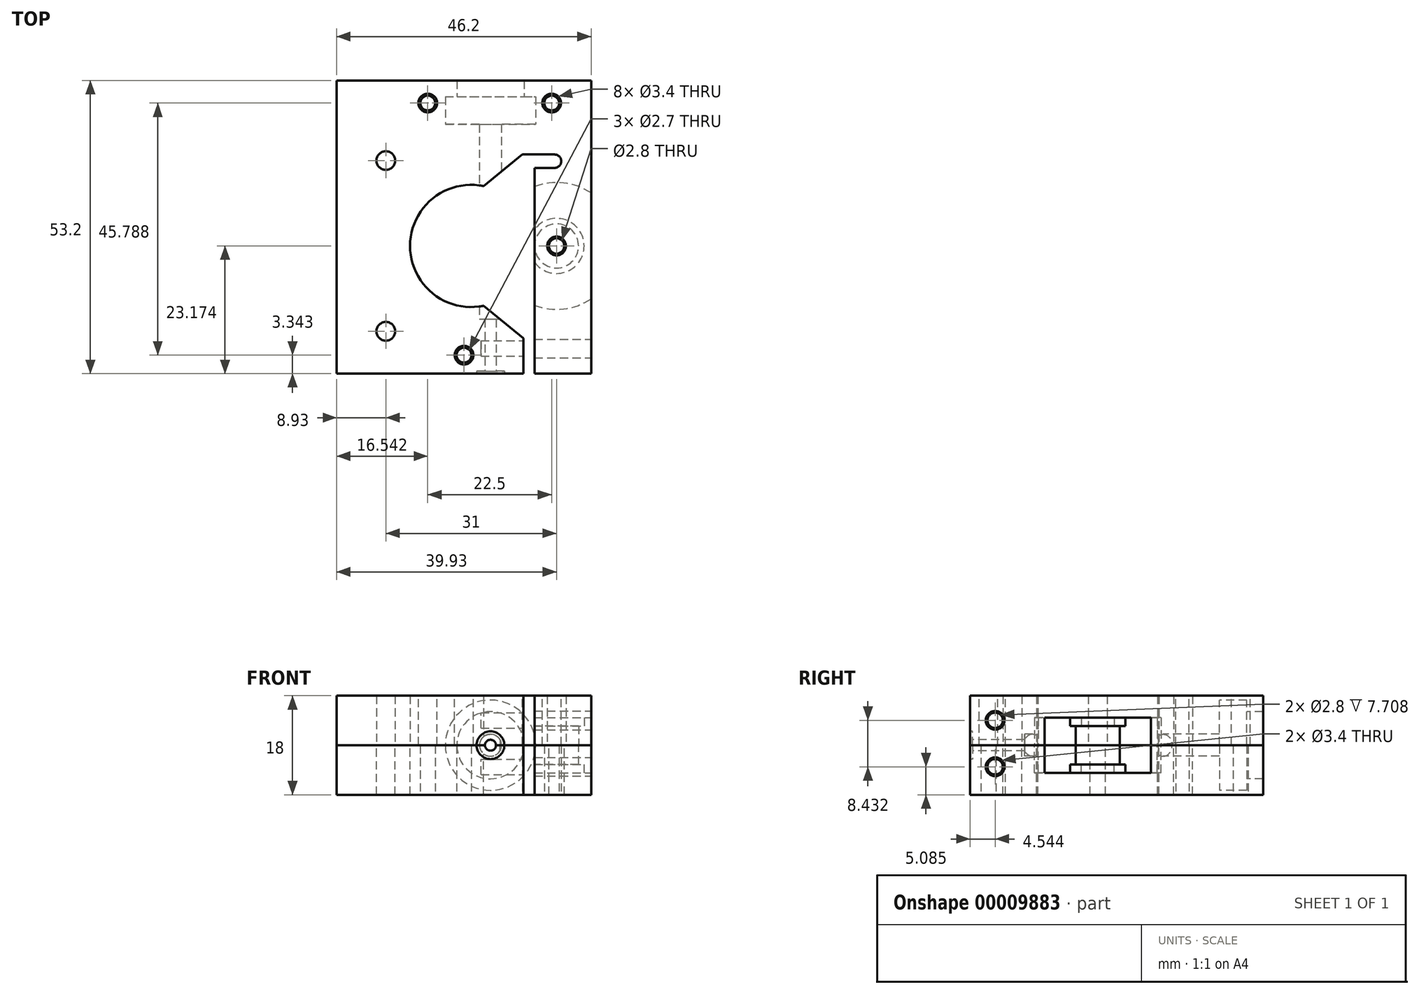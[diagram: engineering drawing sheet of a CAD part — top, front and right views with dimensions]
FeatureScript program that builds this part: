
annotation { "Feature Type Name" : "Feature", "Feature Type Description" : "" }
export const myFeature = defineFeature(function(context is Context, id is Id, definition is map)
    precondition{}
    {
        {
            var Q0;
            Q0=qCreatedBy(makeId("Top.planeOp"),FACE);
            var sketch = newSketch(context, id + "F0", { "sketchPlane" : qUnion([Q0])});
            skLineSegment(sketch, "E0", {"start": v(-24.43, 35.85) * mm, "end": v(-24.43, -17.36) * mm});
            skLineSegment(sketch, "E1", {"start": v(-24.43, -17.36) * mm, "end": v(-24.43, -17.36) * mm});
            skLineSegment(sketch, "E2", {"start": v(-24.43, -17.36) * mm, "end": v(-24.43, -17.35) * mm});
            skLineSegment(sketch, "E3", {"start": v(-24.43, -17.35) * mm, "end": v(9.48, -17.35) * mm});
            skLineSegment(sketch, "E4", {"start": v(9.48, -17.35) * mm, "end": v(9.48, 22.43) * mm});
            skLineSegment(sketch, "E5", {"start": v(9.48, 22.43) * mm, "end": v(15.14, 22.43) * mm});
            skLineSegment(sketch, "E6", {"start": v(15.14, 20) * mm, "end": v(11.48, 20) * mm});
            skLineSegment(sketch, "E7", {"start": v(11.48, 20) * mm, "end": v(11.48, -17.35) * mm});
            skLineSegment(sketch, "E8", {"start": v(11.48, -17.35) * mm, "end": v(21.77, -17.35) * mm});
            skLineSegment(sketch, "E9", {"start": v(21.77, -17.35) * mm, "end": v(21.77, 35.85) * mm});
            skLineSegment(sketch, "E10", {"start": v(21.77, 35.85) * mm, "end": v(-24.43, 35.85) * mm});
            skCircle(sketch, "E11", {"center": v(-7.89, 31.78) * mm, "radius": 1.35 * mm});
            skCircle(sketch, "E12", {"center": v(14.61, 31.78) * mm, "radius": 1.35 * mm});
            skCircle(sketch, "E13", {"center": v(-1.3, -14) * mm, "radius": 1.35 * mm});
            skArc(sketch, "E14", {"start": v(15.14, 20) * mm, "mid": v(16.35, 21.21) * mm, "end": v(15.14, 22.43) * mm});
            skCircle(sketch, "E15", {"center": v(-7.89, 31.78) * mm, "radius": 1.7 * mm});
            skCircle(sketch, "E16", {"center": v(14.61, 31.78) * mm, "radius": 1.7 * mm});
            skCircle(sketch, "E17", {"center": v(-1.3, -14) * mm, "radius": 1.7 * mm});
            skSolve(sketch);
        }
        {
            var Q0;
            Q0=makeQuery(id+"F0.imprint","IMPRINT",FACE,{"disambiguationData":[TD([[makeQuery(id+"F0.imprint","IMPRINT",EDGE,{"derivedFrom":sQuery(id+"F0.wireOp",EDGE,"E0")}),1.0]])]});
            var Q1;
            Q1=makeQuery(id+"F0.imprint","IMPRINT",FACE,{"disambiguationData":[TD([[makeQuery(id+"F0.imprint","IMPRINT",EDGE,{"derivedFrom":sQuery(id+"F0.wireOp",EDGE,"E11")}),-1.0]])]});
            var Q2;
            Q2=makeQuery(id+"F0.imprint","IMPRINT",FACE,{"disambiguationData":[TD([[makeQuery(id+"F0.imprint","IMPRINT",EDGE,{"derivedFrom":sQuery(id+"F0.wireOp",EDGE,"E12")}),-1.0]])]});
            var Q3;
            Q3=makeQuery(id+"F0.imprint","IMPRINT",FACE,{"disambiguationData":[TD([[makeQuery(id+"F0.imprint","IMPRINT",EDGE,{"derivedFrom":sQuery(id+"F0.wireOp",EDGE,"E13")}),-1.0]])]});
            extrude(context, id + "F1", {"entities" : qUnion([Q0, Q1, Q2, Q3]), "depth" : 9 * mm});
        }
        {
            var Q0;
            Q0=makeQuery(id+"F1.opExtrude","CAP_FACE",FACE,{"disambiguationData":[OSD([sQuery(id+"F0.wireOp",EDGE,"E0"),sQuery(id+"F0.wireOp",EDGE,"E1"),sQuery(id+"F0.wireOp",EDGE,"E2"),sQuery(id+"F0.wireOp",EDGE,"E3"),sQuery(id+"F0.wireOp",EDGE,"E4"),sQuery(id+"F0.wireOp",EDGE,"E5"),sQuery(id+"F0.wireOp",EDGE,"E6"),sQuery(id+"F0.wireOp",EDGE,"E7"),sQuery(id+"F0.wireOp",EDGE,"E8"),sQuery(id+"F0.wireOp",EDGE,"E9"),sQuery(id+"F0.wireOp",EDGE,"E10"),sQuery(id+"F0.wireOp",EDGE,"604cad85-587a-4b7d-8070-06f4cba85480"),sQuery(id+"F0.wireOp",EDGE,"6e5e38c1-5bff-4efe-a8c5-b84022f0a049"),sQuery(id+"F0.wireOp",EDGE,"b8144507-9dd7-4af4-87a3-7b649dd00ae6"),sQuery(id+"F0.wireOp",EDGE,"b9c2cb7c-5e58-4995-888e-a78f0403fbb5"),sQuery(id+"F0.wireOp",EDGE,"885990ab-7576-4c23-8475-595d2769e284"),sQuery(id+"F0.wireOp",EDGE,"E11"),sQuery(id+"F0.wireOp",EDGE,"E12"),sQuery(id+"F0.wireOp",EDGE,"E13"),sQuery(id+"F0.wireOp",EDGE,"E14")])],"isStart":false});
            var sketch = newSketch(context, id + "F2", { "sketchPlane" : qUnion([Q0])});
            skCircle(sketch, "E18", {"center": v(0, 5.82) * mm, "radius": 11.1 * mm});
            skCircle(sketch, "E19", {"center": v(-15.5, 21.32) * mm, "radius": 1.7 * mm});
            skCircle(sketch, "E20", {"center": v(-15.5, -9.68) * mm, "radius": 1.7 * mm});
            skSolve(sketch);
        }
        {
            var Q0;
            Q0=qSketchRegion(id+"F2",true);
            extrude(context, id + "F3", {"entities" : qUnion([Q0]), "operationType" : NewBodyOperationType.REMOVE, "endBound" : BoundingType.THROUGH_ALL, "oppositeDirection" : true, "depth" : 25 * mm});
        }
        {
            var Q0;
            Q0=makeQuery(id+"F1.opExtrude","CAP_FACE",FACE,{"disambiguationData":[OSD([sQuery(id+"F0.wireOp",EDGE,"E0"),sQuery(id+"F0.wireOp",EDGE,"E1"),sQuery(id+"F0.wireOp",EDGE,"E2"),sQuery(id+"F0.wireOp",EDGE,"E3"),sQuery(id+"F0.wireOp",EDGE,"E4"),sQuery(id+"F0.wireOp",EDGE,"E5"),sQuery(id+"F0.wireOp",EDGE,"E6"),sQuery(id+"F0.wireOp",EDGE,"E7"),sQuery(id+"F0.wireOp",EDGE,"E8"),sQuery(id+"F0.wireOp",EDGE,"E9"),sQuery(id+"F0.wireOp",EDGE,"E10"),sQuery(id+"F0.wireOp",EDGE,"604cad85-587a-4b7d-8070-06f4cba85480"),sQuery(id+"F0.wireOp",EDGE,"6e5e38c1-5bff-4efe-a8c5-b84022f0a049"),sQuery(id+"F0.wireOp",EDGE,"E11"),sQuery(id+"F0.wireOp",EDGE,"E12"),sQuery(id+"F0.wireOp",EDGE,"E13"),sQuery(id+"F0.wireOp",EDGE,"E14")])],"isStart":false});
            var sketch = newSketch(context, id + "F4", { "sketchPlane" : qUnion([Q0])});
            skCircle(sketch, "E21", {"center": v(15.5, 5.82) * mm, "radius": 11.5 * mm});
            skCircle(sketch, "E22", {"center": v(15.5, 5.82) * mm, "radius": 5 * mm});
            skCircle(sketch, "E23", {"center": v(15.5, 5.82) * mm, "radius": 4 * mm});
            skLineSegment(sketch, "E24", {"start": v(0, 5.82) * mm, "end": v(31, 5.82) * mm, "construction": true});
            skCircle(sketch, "E25", {"center": v(15.5, 5.82) * mm, "radius": 1.4 * mm});
            skCircle(sketch, "E26", {"center": v(15.5, 5.82) * mm, "radius": 1.7 * mm});
            skSolve(sketch);
        }
        {
            var Q0;
            Q0=makeQuery(id+"F4.imprint","IMPRINT",FACE,{"disambiguationData":[TD([[makeQuery(id+"F4.imprint","IMPRINT",EDGE,{"derivedFrom":sQuery(id+"F4.wireOp",EDGE,"E22")}),-1.0]])]});
            extrude(context, id + "F5", {"entities" : qUnion([Q0]), "operationType" : NewBodyOperationType.REMOVE, "oppositeDirection" : true, "depth" : 5 * mm});
        }
        {
            var Q0;
            Q0=makeQuery(id+"F4.imprint","IMPRINT",FACE,{"disambiguationData":[TD([[makeQuery(id+"F4.imprint","IMPRINT",EDGE,{"derivedFrom":sQuery(id+"F4.wireOp",EDGE,"E22")}),1.0]])]});
            var Q1;
            Q1=makeQuery(id+"F4.imprint","IMPRINT",FACE,{"disambiguationData":[TD([[makeQuery(id+"F4.imprint","IMPRINT",EDGE,{"derivedFrom":sQuery(id+"F4.wireOp",EDGE,"E23")}),-1.0]])]});
            extrude(context, id + "F6", {"entities" : qUnion([Q0, Q1]), "operationType" : NewBodyOperationType.REMOVE, "oppositeDirection" : true, "depth" : 3.5 * mm});
        }
        {
            var Q0;
            {var subQ0=sQuery(id+"F0.wireOp",EDGE,"E0");var subQ1=sQuery(id+"F0.wireOp",EDGE,"E1");var subQ2=sQuery(id+"F0.wireOp",EDGE,"E2");var subQ3=sQuery(id+"F0.wireOp",EDGE,"E3");var subQ4=sQuery(id+"F0.wireOp",EDGE,"E4");var subQ5=sQuery(id+"F0.wireOp",EDGE,"E5");var subQ6=sQuery(id+"F0.wireOp",EDGE,"E6");var subQ7=sQuery(id+"F0.wireOp",EDGE,"E7");var subQ8=sQuery(id+"F0.wireOp",EDGE,"E9");var subQ9=sQuery(id+"F0.wireOp",EDGE,"E10");var subQ10=sQuery(id+"F0.wireOp",EDGE,"604cad85-587a-4b7d-8070-06f4cba85480");var subQ11=sQuery(id+"F0.wireOp",EDGE,"6e5e38c1-5bff-4efe-a8c5-b84022f0a049");var subQ12=sQuery(id+"F0.wireOp",EDGE,"E11");var subQ13=sQuery(id+"F0.wireOp",EDGE,"E12");var subQ14=sQuery(id+"F0.wireOp",EDGE,"E13");var subQ15=sQuery(id+"F0.wireOp",EDGE,"E14");Q0=makeQuery(id+"F5.boolean.opBoolean","SPLIT",FACE,{"disambiguationData":[TD([makeQuery(id+"F1.opExtrude","SWEPT_FACE",FACE,{"disambiguationData":[OSD([subQ0])]})])],"derivedFrom":makeQuery(id+"F1.opExtrude","CAP_FACE",FACE,{"disambiguationData":[OSD([subQ0,subQ1,subQ2,subQ3,subQ4,subQ5,subQ6,subQ7,sQuery(id+"F0.wireOp",EDGE,"E8"),subQ8,subQ9,subQ10,subQ11,subQ12,subQ13,subQ14,subQ15])],"isStart":false})});}
            var sketch = newSketch(context, id + "F7", { "sketchPlane" : qUnion([Q0])});
            skLineSegment(sketch, "E27", {"start": v(3.5, 15.43) * mm, "end": v(3.5, 37.1) * mm});
            skLineSegment(sketch, "E28", {"start": v(0, 5.82) * mm, "end": v(31.4, 5.82) * mm, "construction": true});
            skLineSegment(sketch, "E29.0.MirrorCS", {"start": v(0.98, -16.94) * mm, "end": v(2.5, -16.94) * mm});
            skLineSegment(sketch, "E29.1.MirrorCS", {"start": v(3.5, -3.78) * mm, "end": v(3.5, -25.46) * mm});
            skLineSegment(sketch, "E29.2.MirrorCS", {"start": v(0.98, -25.46) * mm, "end": v(0.98, -16.94) * mm});
            skLineSegment(sketch, "E29.3.MirrorCS", {"start": v(1.5, -3.78) * mm, "end": v(3.5, -3.78) * mm});
            skLineSegment(sketch, "E29.4.MirrorCS", {"start": v(2.5, -7.47) * mm, "end": v(1.5, -7.47) * mm});
            skLineSegment(sketch, "E29.5.MirrorCS", {"start": v(2.5, -16.94) * mm, "end": v(2.5, -7.47) * mm});
            skLineSegment(sketch, "E29.6.MirrorCS", {"start": v(3.5, -25.46) * mm, "end": v(0.98, -25.46) * mm});
            skLineSegment(sketch, "E30", {"start": v(-2.6, 37.1) * mm, "end": v(-2.6, 32.9) * mm});
            skLineSegment(sketch, "E31", {"start": v(-2.6, 32.9) * mm, "end": v(-4.7, 32.9) * mm});
            skLineSegment(sketch, "E32", {"start": v(-4.7, 32.9) * mm, "end": v(-4.7, 27.9) * mm});
            skLineSegment(sketch, "E33", {"start": v(-4.7, 27.9) * mm, "end": v(1.5, 27.9) * mm});
            skLineSegment(sketch, "E34", {"start": v(-2.6, 37.1) * mm, "end": v(3.5, 37.1) * mm});
            skLineSegment(sketch, "E35", {"start": v(1.5, 27.9) * mm, "end": v(1.5, 15.43) * mm});
            skLineSegment(sketch, "E36", {"start": v(1.5, 15.43) * mm, "end": v(3.5, 15.43) * mm});
            skLineSegment(sketch, "E37", {"start": v(1.5, -7.47) * mm, "end": v(1.5, -3.78) * mm});
            skSolve(sketch);
        }
        {
            var Q0;
            Q0=qSketchRegion(id+"F7",true);
            var Q1;
            Q1=sQuery(id+"F7.wireOp",EDGE,"E27");
            revolve(context, id + "F8", {"entities" : qUnion([Q0]), "axis" : qUnion([Q1]), "revolveType" : RevolveType.FULL});
        }
        {
            var Q0;
            Q0=makeQuery(id+"F8.opRevolve","SWEPT_BODY",BODY,{"disambiguationData":[OSD([sQuery(id+"F7.wireOp",EDGE,"0e4a01cc-4869-4b9d-8ca2-1c94110d196d"),sQuery(id+"F7.wireOp",EDGE,"4d913e13-2244-4a79-84d2-82f6c5de00b3"),sQuery(id+"F7.wireOp",EDGE,"1203443b-fa58-4cec-9fe4-144960d3b7c2"),sQuery(id+"F7.wireOp",EDGE,"f73e5a92-9274-40af-91db-ab5fa52ec61f"),sQuery(id+"F7.wireOp",EDGE,"4cc6588a-36a6-4115-9f4e-735cf5f17870"),sQuery(id+"F7.wireOp",EDGE,"E27"),sQuery(id+"F7.wireOp",EDGE,"0bbee7b9-97e0-41c3-ac0e-625151f8027d")])]});
            var Q1;
            Q1=makeQuery(id+"F1.opExtrude","SWEPT_BODY",BODY,{"disambiguationData":[OSD([sQuery(id+"F0.wireOp",EDGE,"E0"),sQuery(id+"F0.wireOp",EDGE,"E1"),sQuery(id+"F0.wireOp",EDGE,"E2"),sQuery(id+"F0.wireOp",EDGE,"E3"),sQuery(id+"F0.wireOp",EDGE,"E4"),sQuery(id+"F0.wireOp",EDGE,"E5"),sQuery(id+"F0.wireOp",EDGE,"E6"),sQuery(id+"F0.wireOp",EDGE,"E7"),sQuery(id+"F0.wireOp",EDGE,"E8"),sQuery(id+"F0.wireOp",EDGE,"E9"),sQuery(id+"F0.wireOp",EDGE,"E10"),sQuery(id+"F0.wireOp",EDGE,"604cad85-587a-4b7d-8070-06f4cba85480"),sQuery(id+"F0.wireOp",EDGE,"6e5e38c1-5bff-4efe-a8c5-b84022f0a049"),sQuery(id+"F0.wireOp",EDGE,"E11"),sQuery(id+"F0.wireOp",EDGE,"E12"),sQuery(id+"F0.wireOp",EDGE,"E13"),sQuery(id+"F0.wireOp",EDGE,"E14")])]});
            booleanBodies(context, id + "F9", {"operationType" : BooleanOperationType.SUBTRACTION, "tools" : qUnion([Q0]), "targets" : qUnion([Q1]), "keepTools" : true});
        }
        {
            var Q0;
            Q0=makeQuery(id+"F8.opRevolve","SWEPT_BODY",BODY,{"disambiguationData":[OSD([sQuery(id+"F7.wireOp",EDGE,"E29.0.MirrorCS"),sQuery(id+"F7.wireOp",EDGE,"E29.1.MirrorCS"),sQuery(id+"F7.wireOp",EDGE,"E29.2.MirrorCS"),sQuery(id+"F7.wireOp",EDGE,"E29.3.MirrorCS"),sQuery(id+"F7.wireOp",EDGE,"E29.4.MirrorCS"),sQuery(id+"F7.wireOp",EDGE,"E29.5.MirrorCS"),sQuery(id+"F7.wireOp",EDGE,"E29.6.MirrorCS")])]});
            var Q1;
            Q1=makeQuery(id+"F1.opExtrude","SWEPT_BODY",BODY,{"disambiguationData":[OSD([sQuery(id+"F0.wireOp",EDGE,"E0"),sQuery(id+"F0.wireOp",EDGE,"E1"),sQuery(id+"F0.wireOp",EDGE,"E2"),sQuery(id+"F0.wireOp",EDGE,"E3"),sQuery(id+"F0.wireOp",EDGE,"E4"),sQuery(id+"F0.wireOp",EDGE,"E5"),sQuery(id+"F0.wireOp",EDGE,"E6"),sQuery(id+"F0.wireOp",EDGE,"E7"),sQuery(id+"F0.wireOp",EDGE,"E8"),sQuery(id+"F0.wireOp",EDGE,"E9"),sQuery(id+"F0.wireOp",EDGE,"E10"),sQuery(id+"F0.wireOp",EDGE,"604cad85-587a-4b7d-8070-06f4cba85480"),sQuery(id+"F0.wireOp",EDGE,"6e5e38c1-5bff-4efe-a8c5-b84022f0a049"),sQuery(id+"F0.wireOp",EDGE,"E11"),sQuery(id+"F0.wireOp",EDGE,"E12"),sQuery(id+"F0.wireOp",EDGE,"E13"),sQuery(id+"F0.wireOp",EDGE,"E14")])]});
            booleanBodies(context, id + "F10", {"operationType" : BooleanOperationType.SUBTRACTION, "tools" : qUnion([Q0]), "targets" : qUnion([Q1]), "keepTools" : true});
        }
        {
            var Q0;
            Q0=qSketchRegion(id+"F0",true);
            extrude(context, id + "F11", {"entities" : qUnion([Q0]), "oppositeDirection" : true, "depth" : 9 * mm});
        }
        {
            var Q0;
            Q0=makeQuery(id+"F11.opExtrude","SWEPT_BODY",BODY,{"disambiguationData":[OSD([sQuery(id+"F0.wireOp",EDGE,"E0"),sQuery(id+"F0.wireOp",EDGE,"E3"),sQuery(id+"F0.wireOp",EDGE,"E4"),sQuery(id+"F0.wireOp",EDGE,"E5"),sQuery(id+"F0.wireOp",EDGE,"E6"),sQuery(id+"F0.wireOp",EDGE,"E7"),sQuery(id+"F0.wireOp",EDGE,"E8"),sQuery(id+"F0.wireOp",EDGE,"E9"),sQuery(id+"F0.wireOp",EDGE,"E10"),sQuery(id+"F0.wireOp",EDGE,"E11"),sQuery(id+"F0.wireOp",EDGE,"E12"),sQuery(id+"F0.wireOp",EDGE,"E13"),sQuery(id+"F0.wireOp",EDGE,"E14")])]});
            transform(context, id + "F12", {"entities" : qUnion([Q0]), "transformType" : TransformType.TRANSLATION_3D, "dx" : 0 * mm, "dy" : 0 * mm, "dz" : 18 * mm, "makeCopy" : false});
        }
        {
            var Q0;
            Q0=qSketchRegion(id+"F2",true);
            extrude(context, id + "F13", {"entities" : qUnion([Q0]), "operationType" : NewBodyOperationType.REMOVE, "endBound" : BoundingType.THROUGH_ALL, "depth" : 25 * mm});
        }
        {
            var Q0;
            {var subQ3=sQuery(id+"F4.wireOp",EDGE,"E21");var subQ7=makeQuery(id+"F1.opExtrude","CAP_EDGE",EDGE,{"disambiguationData":[OSD([sQuery(id+"F0.wireOp",EDGE,"E9")])],"isStart":false});var subQ9=makeQuery(id+"F4.imprint","INTERSECT",VERTEX,{"disambiguationData":[OD(0.0)],"derivedFrom":[subQ7,subQ3]});Q0=makeQuery(id+"F4.imprint","IMPRINT",FACE,{"disambiguationData":[TD([[makeQuery(id+"F4.imprint","IMPRINT",EDGE,{"disambiguationData":[TD([[subQ9,-1.0]])],"derivedFrom":subQ3}),1.0]])]});}
            extrude(context, id + "F14", {"entities" : qUnion([Q0]), "operationType" : NewBodyOperationType.REMOVE, "depth" : 5 * mm});
        }
        {
            var Q0;
            Q0=makeQuery(id+"F4.imprint","IMPRINT",FACE,{"disambiguationData":[TD([[makeQuery(id+"F4.imprint","IMPRINT",EDGE,{"derivedFrom":sQuery(id+"F4.wireOp",EDGE,"E23")}),-1.0]])]});
            extrude(context, id + "F15", {"entities" : qUnion([Q0]), "operationType" : NewBodyOperationType.REMOVE, "depth" : 3.5 * mm});
        }
        {
            var Q0;
            Q0=makeQuery(id+"F8.opRevolve","SWEPT_BODY",BODY,{"disambiguationData":[OSD([sQuery(id+"F7.wireOp",EDGE,"0e4a01cc-4869-4b9d-8ca2-1c94110d196d"),sQuery(id+"F7.wireOp",EDGE,"4d913e13-2244-4a79-84d2-82f6c5de00b3"),sQuery(id+"F7.wireOp",EDGE,"1203443b-fa58-4cec-9fe4-144960d3b7c2"),sQuery(id+"F7.wireOp",EDGE,"f73e5a92-9274-40af-91db-ab5fa52ec61f"),sQuery(id+"F7.wireOp",EDGE,"4cc6588a-36a6-4115-9f4e-735cf5f17870"),sQuery(id+"F7.wireOp",EDGE,"E27"),sQuery(id+"F7.wireOp",EDGE,"0bbee7b9-97e0-41c3-ac0e-625151f8027d")])]});
            var Q1;
            Q1=makeQuery(id+"F11.opExtrude","SWEPT_BODY",BODY,{"disambiguationData":[OSD([sQuery(id+"F0.wireOp",EDGE,"E0"),sQuery(id+"F0.wireOp",EDGE,"E3"),sQuery(id+"F0.wireOp",EDGE,"E4"),sQuery(id+"F0.wireOp",EDGE,"E5"),sQuery(id+"F0.wireOp",EDGE,"E6"),sQuery(id+"F0.wireOp",EDGE,"E7"),sQuery(id+"F0.wireOp",EDGE,"E8"),sQuery(id+"F0.wireOp",EDGE,"E9"),sQuery(id+"F0.wireOp",EDGE,"E10"),sQuery(id+"F0.wireOp",EDGE,"E11"),sQuery(id+"F0.wireOp",EDGE,"E12"),sQuery(id+"F0.wireOp",EDGE,"E13"),sQuery(id+"F0.wireOp",EDGE,"E14")])]});
            booleanBodies(context, id + "F16", {"operationType" : BooleanOperationType.SUBTRACTION, "tools" : qUnion([Q0]), "targets" : qUnion([Q1])});
        }
        {
            var Q0;
            Q0=makeQuery(id+"F8.opRevolve","SWEPT_BODY",BODY,{"disambiguationData":[OSD([sQuery(id+"F7.wireOp",EDGE,"E29.0.MirrorCS"),sQuery(id+"F7.wireOp",EDGE,"E29.1.MirrorCS"),sQuery(id+"F7.wireOp",EDGE,"E29.2.MirrorCS"),sQuery(id+"F7.wireOp",EDGE,"E29.3.MirrorCS"),sQuery(id+"F7.wireOp",EDGE,"E29.4.MirrorCS"),sQuery(id+"F7.wireOp",EDGE,"E29.5.MirrorCS"),sQuery(id+"F7.wireOp",EDGE,"E29.6.MirrorCS")])]});
            var Q1;
            Q1=makeQuery(id+"F11.opExtrude","SWEPT_BODY",BODY,{"disambiguationData":[OSD([sQuery(id+"F0.wireOp",EDGE,"E0"),sQuery(id+"F0.wireOp",EDGE,"E3"),sQuery(id+"F0.wireOp",EDGE,"E4"),sQuery(id+"F0.wireOp",EDGE,"E5"),sQuery(id+"F0.wireOp",EDGE,"E6"),sQuery(id+"F0.wireOp",EDGE,"E7"),sQuery(id+"F0.wireOp",EDGE,"E8"),sQuery(id+"F0.wireOp",EDGE,"E9"),sQuery(id+"F0.wireOp",EDGE,"E10"),sQuery(id+"F0.wireOp",EDGE,"E11"),sQuery(id+"F0.wireOp",EDGE,"E12"),sQuery(id+"F0.wireOp",EDGE,"E13"),sQuery(id+"F0.wireOp",EDGE,"E14")])]});
            booleanBodies(context, id + "F17", {"operationType" : BooleanOperationType.SUBTRACTION, "tools" : qUnion([Q0]), "targets" : qUnion([Q1])});
        }
        {
            var Q0;
            Q0=makeQuery(id+"F11.opExtrude","SWEPT_FACE",FACE,{"disambiguationData":[OSD([sQuery(id+"F0.wireOp",EDGE,"E9")])]});
            var sketch = newSketch(context, id + "F18", { "sketchPlane" : qUnion([Q0])});
            skCircle(sketch, "E38", {"center": v(-12.8, 13.52) * mm, "radius": 1.7 * mm});
            skCircle(sketch, "E39", {"center": v(-12.8, 13.52) * mm, "radius": 1.4 * mm});
            skCircle(sketch, "E40", {"center": v(-12.8, 5.09) * mm, "radius": 1.7 * mm});
            skCircle(sketch, "E41", {"center": v(-12.8, 5.09) * mm, "radius": 1.4 * mm});
            skSolve(sketch);
        }
        {
            var Q0;
            Q0=makeQuery(id+"F18.imprint","IMPRINT",FACE,{"disambiguationData":[TD([[makeQuery(id+"F18.imprint","IMPRINT",EDGE,{"derivedFrom":sQuery(id+"F18.wireOp",EDGE,"E39")}),1.0]])]});
            extrude(context, id + "F19", {"entities" : qUnion([Q0]), "operationType" : NewBodyOperationType.REMOVE, "oppositeDirection" : true, "depth" : 20 * mm});
        }
        {
            var Q0;
            Q0=makeQuery(id+"F18.imprint","IMPRINT",FACE,{"disambiguationData":[TD([[makeQuery(id+"F18.imprint","IMPRINT",EDGE,{"derivedFrom":sQuery(id+"F18.wireOp",EDGE,"E38")}),1.0]])]});
            extrude(context, id + "F20", {"entities" : qUnion([Q0]), "operationType" : NewBodyOperationType.REMOVE, "oppositeDirection" : true, "depth" : 11 * mm});
        }
        {
            var Q0;
            Q0=makeQuery(id+"F18.imprint","IMPRINT",FACE,{"disambiguationData":[TD([[makeQuery(id+"F18.imprint","IMPRINT",EDGE,{"derivedFrom":sQuery(id+"F18.wireOp",EDGE,"E41")}),1.0]])]});
            extrude(context, id + "F21", {"entities" : qUnion([Q0]), "operationType" : NewBodyOperationType.REMOVE, "oppositeDirection" : true, "depth" : 20 * mm});
        }
        {
            var Q0;
            Q0=makeQuery(id+"F18.imprint","IMPRINT",FACE,{"disambiguationData":[TD([[makeQuery(id+"F18.imprint","IMPRINT",EDGE,{"derivedFrom":sQuery(id+"F18.wireOp",EDGE,"E40")}),1.0]])]});
            extrude(context, id + "F22", {"entities" : qUnion([Q0]), "operationType" : NewBodyOperationType.REMOVE, "oppositeDirection" : true, "depth" : 11 * mm});
        }
        {
            var Q0;
            Q0=makeQuery(id+"F4.imprint","IMPRINT",FACE,{"disambiguationData":[TD([[makeQuery(id+"F4.imprint","IMPRINT",EDGE,{"derivedFrom":sQuery(id+"F4.wireOp",EDGE,"E25")}),1.0]])]});
            extrude(context, id + "F23", {"entities" : qUnion([Q0]), "operationType" : NewBodyOperationType.REMOVE, "endBound" : BoundingType.THROUGH_ALL, "oppositeDirection" : true, "depth" : 25 * mm});
        }
        {
            var Q0;
            Q0=makeQuery(id+"F4.imprint","IMPRINT",FACE,{"disambiguationData":[TD([[makeQuery(id+"F4.imprint","IMPRINT",EDGE,{"derivedFrom":sQuery(id+"F4.wireOp",EDGE,"E25")}),1.0]])]});
            var Q1;
            Q1=makeQuery(id+"F4.imprint","IMPRINT",FACE,{"disambiguationData":[TD([[makeQuery(id+"F4.imprint","IMPRINT",EDGE,{"derivedFrom":sQuery(id+"F4.wireOp",EDGE,"E25")}),-1.0]])]});
            extrude(context, id + "F24", {"entities" : qUnion([Q0, Q1]), "operationType" : NewBodyOperationType.REMOVE, "endBound" : BoundingType.THROUGH_ALL, "depth" : 25 * mm});
        }
        {
            var Q0;
            Q0=makeQuery(id+"F3.boolean.opBoolean","INTERSECT",EDGE,{"disambiguationData":[OD(0.0)],"derivedFrom":[makeQuery(id+"F1.opExtrude","SWEPT_FACE",FACE,{"disambiguationData":[OSD([sQuery(id+"F0.wireOp",EDGE,"E4")])]}),makeQuery(id+"F3.opExtrude","SWEPT_FACE",FACE,{"disambiguationData":[OSD([sQuery(id+"F2.wireOp",EDGE,"E18")])]})]});
            var Q1;
            Q1=makeQuery(id+"F3.boolean.opBoolean","INTERSECT",EDGE,{"disambiguationData":[OD(1.0)],"derivedFrom":[makeQuery(id+"F1.opExtrude","SWEPT_FACE",FACE,{"disambiguationData":[OSD([sQuery(id+"F0.wireOp",EDGE,"E4")])]}),makeQuery(id+"F3.opExtrude","SWEPT_FACE",FACE,{"disambiguationData":[OSD([sQuery(id+"F2.wireOp",EDGE,"E18")])]})]});
            var Q2;
            Q2=makeQuery(id+"F13.boolean.opBoolean","INTERSECT",EDGE,{"disambiguationData":[OD(1.0)],"derivedFrom":[makeQuery(id+"F11.opExtrude","SWEPT_FACE",FACE,{"disambiguationData":[OSD([sQuery(id+"F0.wireOp",EDGE,"E4")])]}),makeQuery(id+"F13.opExtrude","SWEPT_FACE",FACE,{"disambiguationData":[OSD([sQuery(id+"F2.wireOp",EDGE,"E18")])]})]});
            var Q3;
            Q3=makeQuery(id+"F13.boolean.opBoolean","INTERSECT",EDGE,{"disambiguationData":[OD(0.0)],"derivedFrom":[makeQuery(id+"F11.opExtrude","SWEPT_FACE",FACE,{"disambiguationData":[OSD([sQuery(id+"F0.wireOp",EDGE,"E4")])]}),makeQuery(id+"F13.opExtrude","SWEPT_FACE",FACE,{"disambiguationData":[OSD([sQuery(id+"F2.wireOp",EDGE,"E18")])]})]});
            chamfer(context, id + "F25", {"entities" : qUnion([Q0, Q1, Q2, Q3]), "width" : 6 * mm, "tangentPropagation" : true});
        }
    });
